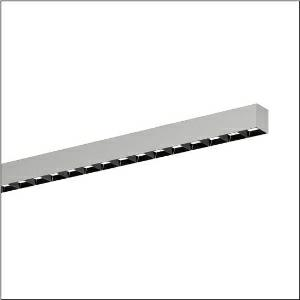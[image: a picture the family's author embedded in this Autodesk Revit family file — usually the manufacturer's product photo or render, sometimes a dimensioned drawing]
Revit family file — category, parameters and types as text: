
# Revit family: silica_21_51mx21dc3asb
name_source: partatom
category: Lighting Fixtures
units: mm (PartAtom-declared; Revit-internal decimal feet)

## family parameters
Cut with Voids When Loaded = No
Host = Face
Light Source = No
Part Type = Normal
Room Calculation Point = No
Round Connector Dimension = Use Diameter
Shared = No

## types (1)
- --- (1 x LED, 10800 lm, 69.3 W, 3000K)
    Apparent Load = 69 VA
    CIE Flux Codes = 87 99 100 100 100
    Color Rendering = 80
    Color Temperature = 3000K
    Default Elevation = 1800 mm
    Description = Silica 21, office luminaire, primary light control with darklight reflector, of PMMA, black, CAT 2 (L<= 3000cd/m²), light emission: direct distribution, primary light characteristic: symmetric, installation type: surface-mounted, LED, rated luminous flux: 10.800lm, luminous efficacy: 156lm/W, light colour: 830, colour temperature: 3000K, control gear: DALI 2, with terminal, 3+2-pole, max. 2.5mm², mains connection: 220..240V, AC, 50/60Hz, luminaire housing, of aluminium, metallic grey (RAL 9006), length: 3.004mm, width: 53mm, height: 53mm, protection rating (complete): IP20, insulation class (complete): insulation class I (protective earthing), certification: CE, permissible operating ambient temperature: 0..+35°C, standard: EN 50419, packaging unit: 1 piece
    Height = 53 mm
    Lamp = 1 x LED
    Lamp Light Flux = 10800 lm
    Lamp Power = 69.3 W
    Lamp count = 1
    Length = 3004 mm
    Luminous efficacy = 156 lm/W
    Manufacturer = Siteco
    ModVariant = No
    Model = 51MX21DC3ASB
    Mounting Place = Ceiling
    Mounting Type = Surface mounted
    Number of Poles = 1
    OnlyDefault = Yes
    Power Factor = 1
    Product Name = Silica 21
    Product group = office luminaire | ceiling mounted
    ProductGroupID = 301
    Protection Class = Protection class I
    Protection Degree = IP 20
    RLX_Detail_Level = 1
    RLX_Emergency_Light_Flux = 0 lm
    RLX_Emergency_Type = 0
    RLX_Emergency_Type_DB = No
    RlxData = <blob elided: 62585 chars, md5=12761c09>
    Socket = socket
    Standby Power = 0 W
    System Light Flux = 10800 lm
    System Power = 69 W
    Type Comments = factory setting: luminous flux: 100 % | dim-lin: 254 | 393 mA
    Type Image = l_1335929.jpg
    URL = http://relux.com
    VarID = @adj_123663
    Voltage = 0 V
    Weight = 0.00 kg
    Width = 53 mm

## geometry (parser evidence)
native form markers: Blend x4, Sweep x10
no freeform markers — native parametric forms only
